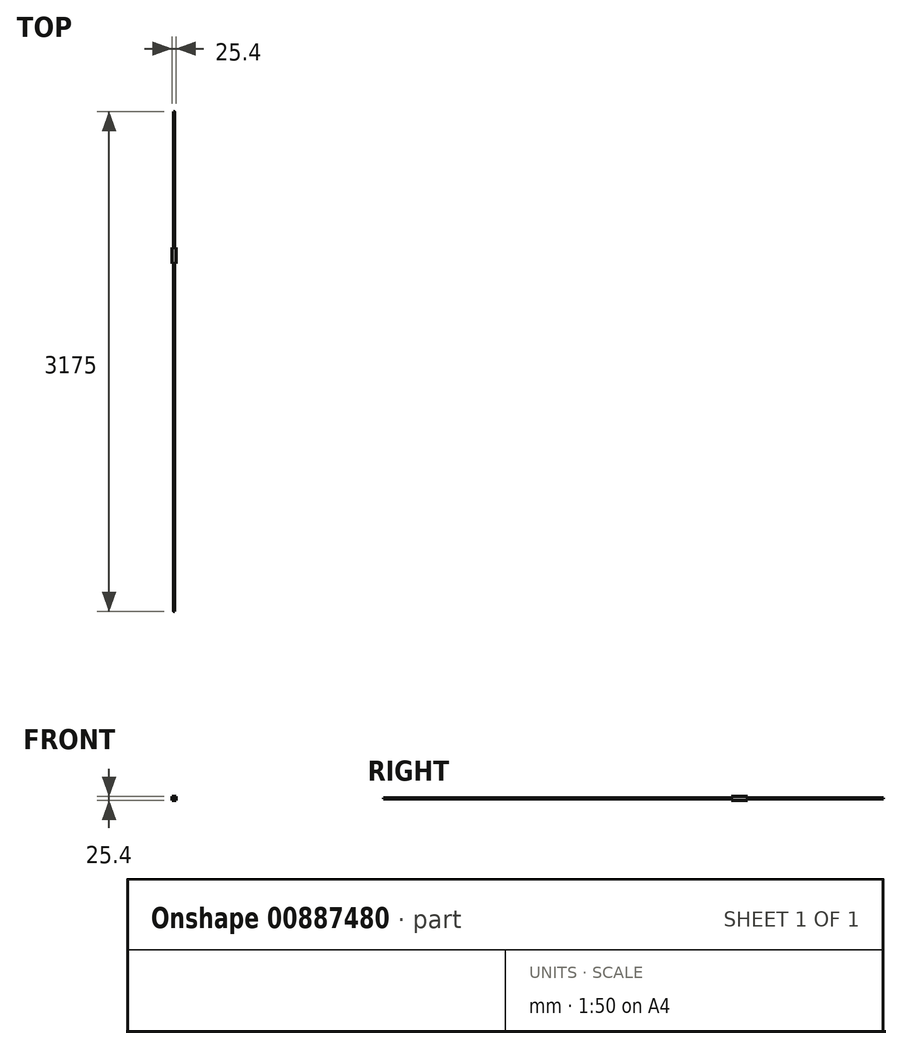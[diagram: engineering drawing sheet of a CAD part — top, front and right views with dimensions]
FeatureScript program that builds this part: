
annotation { "Feature Type Name" : "Feature", "Feature Type Description" : "" }
export const myFeature = defineFeature(function(context is Context, id is Id, definition is map)
    precondition{}
    {
        {
            var Q0;
            Q0=qCreatedBy(makeId("Front.planeOp"),FACE);
            var sketch = newSketch(context, id + "F0", { "sketchPlane" : qUnion([Q0])});
            skCircle(sketch, "E0", {"center": v(0, 0) * mm, "radius": 3.18 * mm});
            skSolve(sketch);
        }
        {
            var Q0;
            Q0=makeQuery(id+"F0.imprint","IMPRINT",FACE,{"disambiguationData":[TD([[makeQuery(id+"F0.imprint","IMPRINT",EDGE,{"derivedFrom":sQuery(id+"F0.wireOp",EDGE,"E0")}),1.0]])]});
            extrude(context, id + "F1", {"entities" : qUnion([Q0]), "depth" : 3175 * mm, "offsetDistance" : 25.4 * mm});
        }
        {
            var Q0;
            Q0=qCreatedBy(makeId("Front.planeOp"),FACE);
            cPlane(context, id + "F2", {"entities" : qUnion([Q0]), "cplaneType" : CPlaneType.OFFSET, "offset" : 914.4 * mm, "width" : 152.4 * mm, "height" : 152.4 * mm});
        }
        {
            var Q0;
            Q0=qCreatedBy(id+"F2.planeOp",FACE);
            var sketch = newSketch(context, id + "F3", { "sketchPlane" : qUnion([Q0])});
            skLineSegment(sketch, "E1.bottom", {"start": v(-12.7, 12.7) * mm, "end": v(12.7, 12.7) * mm});
            skLineSegment(sketch, "E1.top", {"start": v(-12.7, -12.7) * mm, "end": v(12.7, -12.7) * mm});
            skLineSegment(sketch, "E1.left", {"start": v(-12.7, 12.7) * mm, "end": v(-12.7, -12.7) * mm});
            skLineSegment(sketch, "E1.right", {"start": v(12.7, 12.7) * mm, "end": v(12.7, -12.7) * mm});
            skSolve(sketch);
        }
        {
            var Q0;
            Q0=makeQuery(id+"F3.imprint","IMPRINT",FACE,{"disambiguationData":[TD([[makeQuery(id+"F3.imprint","IMPRINT",EDGE,{"derivedFrom":sQuery(id+"F3.wireOp",EDGE,"E1.bottom")}),-1.0]])]});
            extrude(context, id + "F4", {"entities" : qUnion([Q0]), "operationType" : NewBodyOperationType.ADD, "depth" : 50.8 * mm, "offsetDistance" : 25.4 * mm, "hasSecondDirection" : true, "secondDirectionOppositeDirection" : true, "secondDirectionDepth" : 50.8 * mm});
        }
    });
